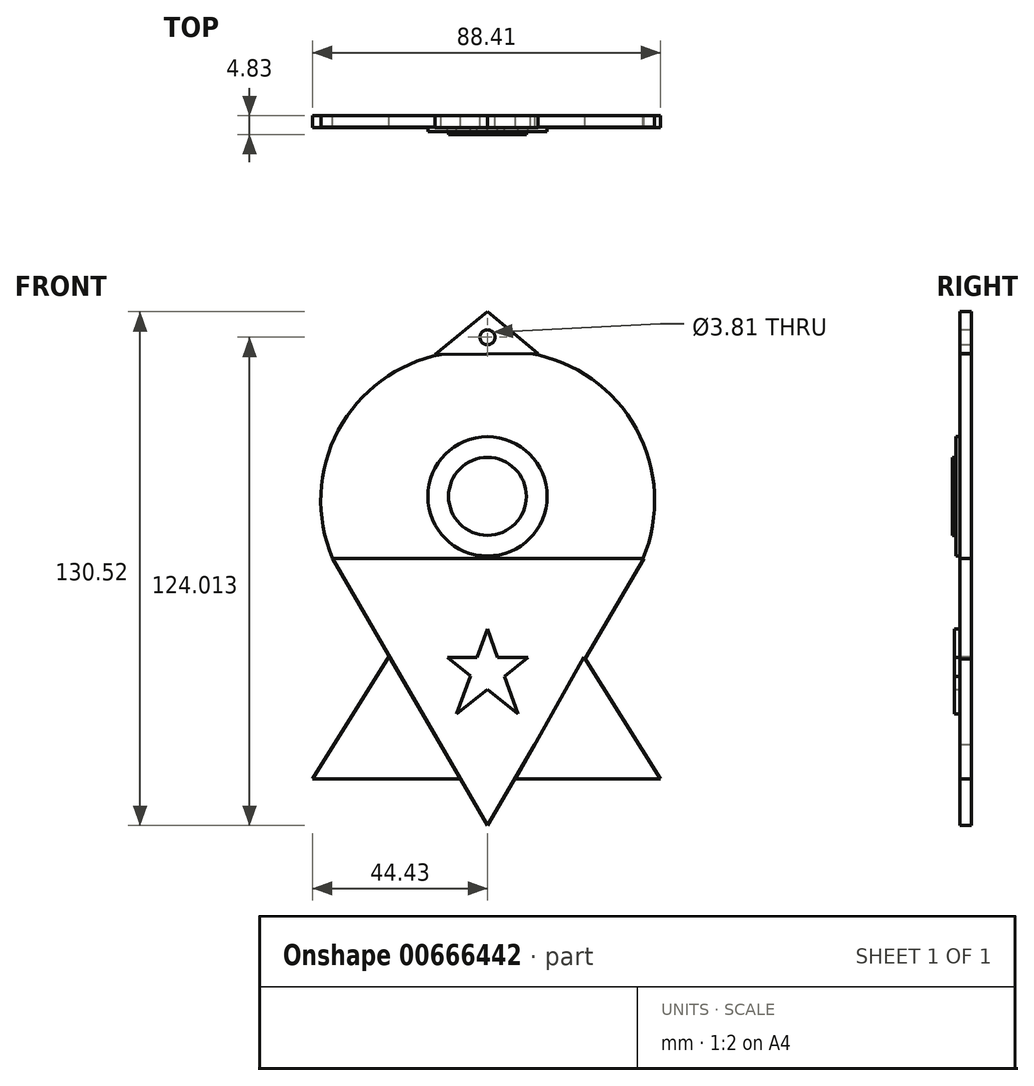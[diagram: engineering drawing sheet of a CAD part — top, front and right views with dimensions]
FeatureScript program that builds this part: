
annotation { "Feature Type Name" : "Feature", "Feature Type Description" : "" }
export const myFeature = defineFeature(function(context is Context, id is Id, definition is map)
    precondition{}
    {
        {
            var Q0;
            Q0=qCreatedBy(makeId("Front.planeOp"),FACE);
            var sketch = newSketch(context, id + "F0", { "sketchPlane" : qUnion([Q0])});
            skLineSegment(sketch, "E0", {"start": v(-39.4, 0) * mm, "end": v(0, -67.85) * mm});
            skLineSegment(sketch, "E1", {"start": v(0, -67.85) * mm, "end": v(39.76, 0) * mm});
            skLineSegment(sketch, "E2", {"start": v(-39.4, 0) * mm, "end": v(0, 0) * mm});
            skLineSegment(sketch, "E3", {"start": v(0, 0) * mm, "end": v(39.76, 0) * mm});
            skSolve(sketch);
        }
        {
            var Q0;
            Q0=qCreatedBy(makeId("Front.planeOp"),FACE);
            var sketch = newSketch(context, id + "F1", { "sketchPlane" : qUnion([Q0])});
            skArc(sketch, "E4", {"start": v(0, 52.3) * mm, "mid": v(-34.72, 37.46) * mm, "end": v(-39.4, 0) * mm});
            skArc(sketch, "E5", {"start": v(39.54, 0) * mm, "mid": v(34.82, 37.52) * mm, "end": v(0, 52.3) * mm});
            skLineSegment(sketch, "E6", {"start": v(-39.4, 0) * mm, "end": v(0, 0) * mm});
            skLineSegment(sketch, "E7", {"start": v(0, 0) * mm, "end": v(39.54, 0) * mm});
            skSolve(sketch);
        }
        {
            var Q0;
            Q0=qSketchRegion(id+"F1",true);
            var Q1;
            Q1=qSketchRegion(id+"F0",true);
            extrude(context, id + "F2", {"entities" : qUnion([Q0, Q1]), "depth" : 3 * mm, "offsetDistance" : 25.4 * mm});
        }
        {
            var Q0;
            Q0=qCreatedBy(makeId("Front.planeOp"),FACE);
            var sketch = newSketch(context, id + "F3", { "sketchPlane" : qUnion([Q0])});
            skLineSegment(sketch, "E8", {"start": v(-7.8, -39.57) * mm, "end": v(0, -17.96) * mm});
            skLineSegment(sketch, "E9", {"start": v(0, -17.96) * mm, "end": v(7.7, -39.57) * mm});
            skLineSegment(sketch, "E10", {"start": v(7.7, -39.57) * mm, "end": v(-10.2, -25.16) * mm});
            skLineSegment(sketch, "E11", {"start": v(-10.2, -25.16) * mm, "end": v(10.32, -25.16) * mm});
            skLineSegment(sketch, "E12", {"start": v(10.32, -25.16) * mm, "end": v(-7.8, -39.57) * mm});
            skSolve(sketch);
        }
        {
            var Q0;
            Q0=qSketchRegion(id+"F3",true);
            extrude(context, id + "F4", {"entities" : qUnion([Q0]), "operationType" : NewBodyOperationType.ADD, "depth" : 4.32 * mm, "offsetDistance" : 25.4 * mm});
        }
        {
            var Q0;
            Q0=qCreatedBy(makeId("Front.planeOp"),FACE);
            var sketch = newSketch(context, id + "F5", { "sketchPlane" : qUnion([Q0])});
            skCircle(sketch, "E13", {"center": v(0, 15.74) * mm, "radius": 15.16 * mm});
            skSolve(sketch);
        }
        {
            var Q0;
            Q0=qSketchRegion(id+"F5",true);
            extrude(context, id + "F6", {"entities" : qUnion([Q0]), "operationType" : NewBodyOperationType.ADD, "depth" : 4.06 * mm, "offsetDistance" : 25.4 * mm});
        }
        {
            var Q0;
            Q0=makeQuery(id+"F6.opExtrude","CAP_FACE",FACE,{"disambiguationData":[OSD([sQuery(id+"F5.wireOp",EDGE,"E13")])],"isStart":false});
            var sketch = newSketch(context, id + "F7", { "sketchPlane" : qUnion([Q0])});
            skCircle(sketch, "E14", {"center": v(0, 15.74) * mm, "radius": 9.9 * mm});
            skSolve(sketch);
        }
        {
            var Q0;
            Q0=makeQuery(id+"F7.imprint","IMPRINT",FACE,{"disambiguationData":[TD([[makeQuery(id+"F7.imprint","IMPRINT",EDGE,{"derivedFrom":sQuery(id+"F7.wireOp",EDGE,"E14")}),1.0]])]});
            extrude(context, id + "F8", {"entities" : qUnion([Q0]), "operationType" : NewBodyOperationType.ADD, "depth" : 0.76 * mm, "offsetDistance" : 25.4 * mm});
        }
        {
            var Q0;
            Q0=qCreatedBy(makeId("Front.planeOp"),FACE);
            var sketch = newSketch(context, id + "F9", { "sketchPlane" : qUnion([Q0])});
            skLineSegment(sketch, "E15", {"start": v(-13.34, 51.83) * mm, "end": v(0, 62.67) * mm});
            skLineSegment(sketch, "E16", {"start": v(0, 62.67) * mm, "end": v(12.88, 52.05) * mm});
            skLineSegment(sketch, "E17", {"start": v(12.88, 52.05) * mm, "end": v(-13.34, 51.83) * mm});
            skSolve(sketch);
        }
        {
            var Q0;
            Q0=makeQuery(id+"F9.imprint","IMPRINT",FACE,{"disambiguationData":[TD([[makeQuery(id+"F9.imprint","IMPRINT",EDGE,{"derivedFrom":sQuery(id+"F9.wireOp",EDGE,"E15")}),-1.0]])]});
            extrude(context, id + "F10", {"entities" : qUnion([Q0]), "operationType" : NewBodyOperationType.ADD, "depth" : 3.05 * mm, "offsetDistance" : 25.4 * mm});
        }
        {
            var Q0;
            Q0=qCreatedBy(makeId("Front.planeOp"),FACE);
            var sketch = newSketch(context, id + "F11", { "sketchPlane" : qUnion([Q0])});
            skPoint(sketch, "E18", {"position": v(0, 56.16) * mm});
            skSolve(sketch);
        }
        {
            var Q0;
            Q0=sQuery(id+"F11.wireOp",VERTEX,"E18");
            var Q1;
            Q1=makeQuery(id+"F2.opExtrude","SWEPT_BODY",BODY,{"disambiguationData":[OSD([sQuery(id+"F1.wireOp",EDGE,"E4"),sQuery(id+"F1.wireOp",EDGE,"E5"),sQuery(id+"F1.wireOp",EDGE,"E6"),sQuery(id+"F1.wireOp",EDGE,"E7")])]});
            hole(context, id + "F12", {"style" : HoleStyle.SIMPLE, "endStyle" : HoleEndStyle.THROUGH, "oppositeDirection" : true, "holeDiameter" : 3.8 * mm, "majorDiameter" : 6.35 * mm, "isTappedThrough" : true, "tappedDepth" : 12.7 * mm, "tapClearance" : 3, "locations" : qUnion([Q0]), "scope" : qUnion([Q1])});
        }
        {
            var Q0;
            Q0=qCreatedBy(makeId("Front.planeOp"),FACE);
            var sketch = newSketch(context, id + "F13", { "sketchPlane" : qUnion([Q0])});
            skLineSegment(sketch, "E19", {"start": v(24.55, -25.09) * mm, "end": v(43.98, -56.08) * mm});
            skLineSegment(sketch, "E20", {"start": v(43.98, -56.08) * mm, "end": v(7.1, -56.08) * mm});
            skLineSegment(sketch, "E21", {"start": v(7.1, -56.08) * mm, "end": v(24.55, -25.09) * mm});
            skSolve(sketch);
        }
        {
            var Q0;
            Q0=qSketchRegion(id+"F13",true);
            extrude(context, id + "F14", {"entities" : qUnion([Q0]), "operationType" : NewBodyOperationType.ADD, "depth" : 3.05 * mm, "offsetDistance" : 25.4 * mm});
        }
        {
            var Q0;
            Q0=qCreatedBy(makeId("Front.planeOp"),FACE);
            var sketch = newSketch(context, id + "F15", { "sketchPlane" : qUnion([Q0])});
            skLineSegment(sketch, "E22", {"start": v(-25, -24.87) * mm, "end": v(-44.43, -56.08) * mm});
            skLineSegment(sketch, "E23", {"start": v(-44.43, -56.08) * mm, "end": v(-6.88, -56.08) * mm});
            skLineSegment(sketch, "E24", {"start": v(-6.88, -56.08) * mm, "end": v(-25, -24.87) * mm});
            skSolve(sketch);
        }
        {
            var Q0;
            Q0=qSketchRegion(id+"F15",true);
            extrude(context, id + "F16", {"entities" : qUnion([Q0]), "depth" : 3.05 * mm, "offsetDistance" : 25.4 * mm});
        }
    });
